# Revit family: Indoor_Table Lamp_Santa&Cole_Básica Mínima
name_source: partatom
category: Luminarias
revit_build: Autodesk Revit 2018 (Build: 20190510_1515(x64)
units: mm (PartAtom-declared; Revit-internal decimal feet)

## family parameters
Compartido = No
Corte con vacíos al cargar = No
Cota de conector redondo = Diámetro de uso
Número OmniClass = 23.80.70.00
Origen de luz = Sí
Punto de cálculo de habitación = No
Se basa en plano de trabajo = No
Siempre vertical = Sí
Tipo de pieza = Normal
Título OmniClass = Lighting

## types (2) — shared parameters
Assembly instructions - CE = https://www.santacole.com
Assembly instructions - UL = https://www.santacole.com
Cambio de temperatura de color de luz atenuada = <Ninguno>
Carga aparente = 6 VA
Code = BAM01/BAM12
Energy Label = https://www.santacole.com
Fabricante = Santa & Cole
Filtro de color = 16777215
Load = 6 W
Manufacturer website = http://www.santacole.com
Modelo = Básica Mínima
Tamaño de símbolo de origen de luz = 50 mm
Technical Information = https://www.santacole.com
URL = https://www.santacole.com

## per-type parameters (varying)
| type | Base Material | Visibility_Beige Parchment |
| Beige Parchment lampshade and bronze base | Santa & Cole - Bronze | Sí |
| Natural ribbon lampshade and nickel base | Santa & Cole - Nickel | No |

## geometry (parser evidence)
native form markers: Sweep x3
no freeform markers — native parametric forms only
